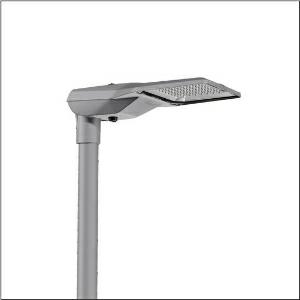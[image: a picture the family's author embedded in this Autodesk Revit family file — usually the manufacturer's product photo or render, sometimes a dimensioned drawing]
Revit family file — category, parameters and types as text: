
# Revit family: streetlight_sl_21_midi___stw1_0a_5xe3e43t08lb_2539
name_source: partatom
category: Lighting Fixtures
units: mm (PartAtom-declared; Revit-internal decimal feet)

## family parameters
Cut with Voids When Loaded = No
Host = Face
Light Source = No
Part Type = Normal
Room Calculation Point = No
Round Connector Dimension = Use Diameter
Shared = No

## types (1)
- --- (1 x LED, 14950 lm, 99.6 W, 4000K)
    Apparent Load = 100 VA
    CIE Flux Codes = 38 75 98 100 100
    Color Rendering = 70
    Color Temperature = 4000K
    Default Elevation = 1800 mm
    Description = Streetlight SL 21 midi, mast luminaire, primary light control with lens, of PMMA, primary optical cover: cover, of toughened safety glass, transparent, light distribution: STW1.0a, light emission: direct distribution, primary light characteristic: asymmetric, installation type: side-entry, post-top, LED, High Power LED, rated luminous flux: 14.950lm, luminous efficacy: 150lm/W, light colour: 740, colour temperature: 4000K, control gear: D4i, control: overheat protection, constant luminous flux control, time-dependent luminous flux control, flexible luminous flux parameterisation, pre-setting: logarithmic dimming characteristic, mains connection: 230..240V, AC, 50/60Hz, start of lifetime: 100W, end of service life: 102W, reduction: 46W, luminaire housing, of diecast aluminium, powder-coated, Siteco® metallic grey (DB 702S), corrosivity category C5 mid according to DIN EN ISO 12944, please order mast flange separately, inclination adjustable: 0°, 5°, 10°, 15°, sealing non-destructively replaceable, multi-level sealing system, length: 644mm, width: 335mm, height: 110mm, mast flange for spigot size: 42mm (side-entry): 5XC10008XM4, 60/48mm (side-entry/post-top): 5XC10108XM2, 76/60mm (side-entry/post-top): 5XC10108XM1, mounting height: 4..8m, Smart Interface below and above, protection rating (complete): IP66, insulation class (complete): insulation class II (safety insulation), certification: CE, ENEC, ENEC+, VDE, impact resistance: IK10, permissible operating ambient temperature for outdoor applications: -40..+50°C, standard-compliant lighting for roads and squares, packaging unit: 1 piece

Light Distribution: STW1.0a
    Height = 111 mm
    Lamp = 1 x LED
    Lamp Light Flux = 14950 lm
    Lamp Power = 99.6 W
    Lamp count = 1
    Length = 644 mm
    Luminous efficacy = 150 lm/W
    Manufacturer = Siteco
    ModVariant = No
    Model = 5XE3E43T08LB
    Number of Poles = 1
    OnlyDefault = Yes
    Power Factor = 1
    Product Name = Streetlight SL 21 midi | STW1.0a
    Product group = mast luminaire | pylon top
    ProductGroupID = 6100
    Protection Class = Protection class II
    Protection Degree = IP 66
    RLX_Detail_Level = 1
    RLX_Emergency_Light_Flux = 0 lm
    RLX_Emergency_Type = 0
    RLX_Emergency_Type_DB = No
    RlxData = <blob elided: 26989 chars, md5=d8483cc9>
    Socket = socket
    Standby Power = 0 W
    System Light Flux = 14950 lm
    System Power = 100 W
    Type Comments = factory setting: luminous flux: 100 % | dim-lin: 254 | 1020 mA
    Type Image = l_1004304.jpg
    URL = http://relux.com
    VarID = @adj_031781
    Voltage = 0 V
    Weight = 0.00 kg
    Width = 336 mm

## geometry (parser evidence)
native form markers: Blend x4, Sweep x10
no freeform markers — native parametric forms only
